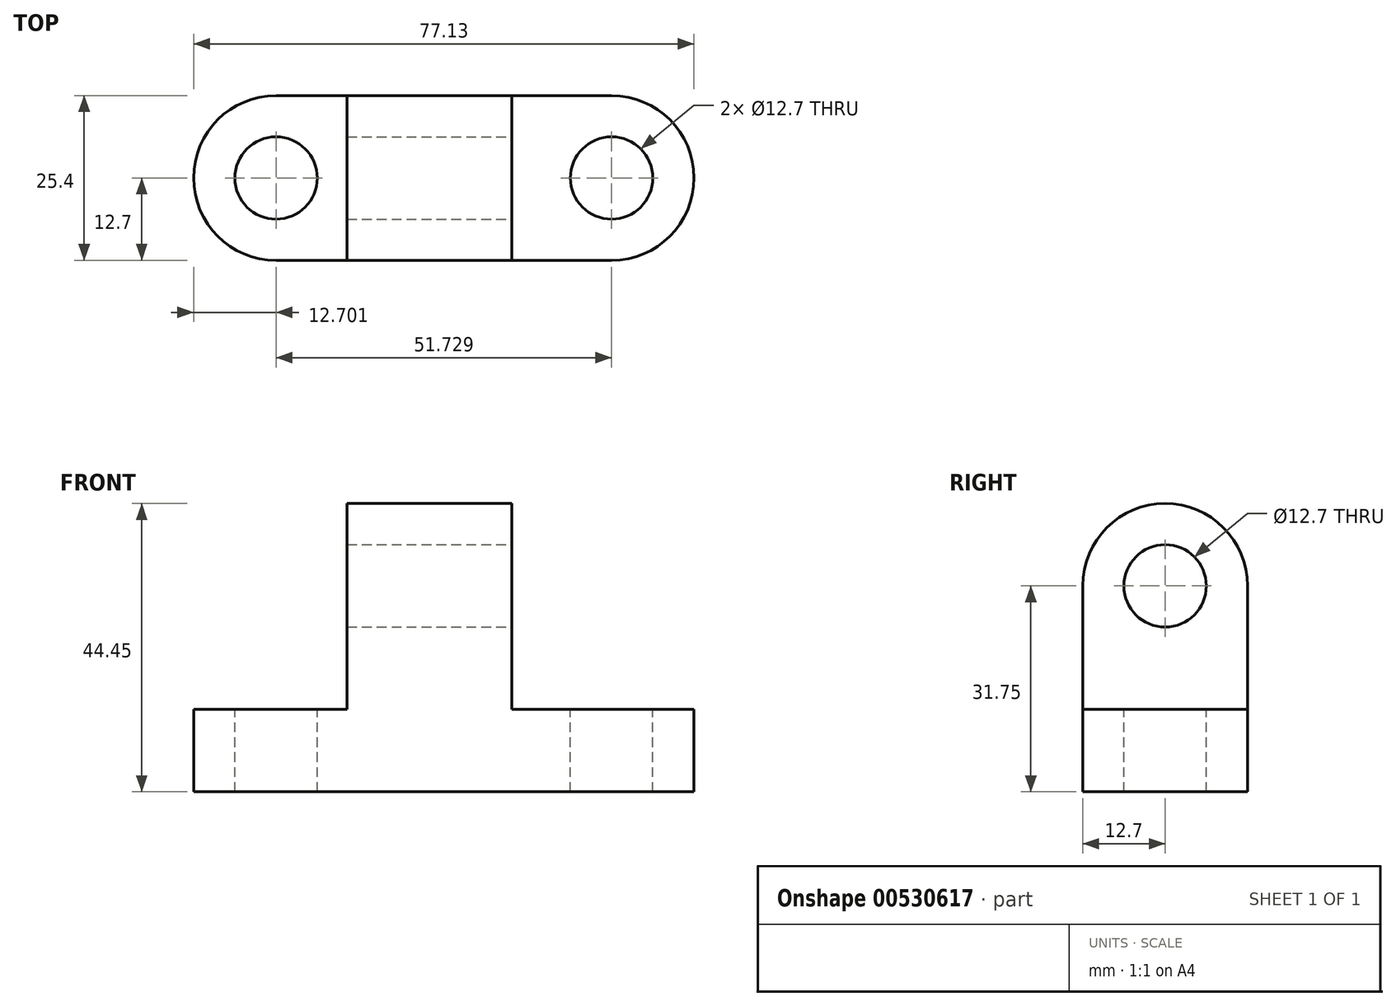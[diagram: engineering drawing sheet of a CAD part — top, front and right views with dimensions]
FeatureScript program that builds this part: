
annotation { "Feature Type Name" : "Feature", "Feature Type Description" : "" }
export const myFeature = defineFeature(function(context is Context, id is Id, definition is map)
    precondition{}
    {
        {
            var Q0;
            Q0=qCreatedBy(makeId("Front.planeOp"),FACE);
            var sketch = newSketch(context, id + "F0", { "sketchPlane" : qUnion([Q0])});
            skLineSegment(sketch, "E0", {"start": v(0, 0) * mm, "end": v(-51.73, 0) * mm});
            skLineSegment(sketch, "E1", {"start": v(-51.73, 0) * mm, "end": v(-51.73, 12.7) * mm});
            skLineSegment(sketch, "E2", {"start": v(-51.73, 12.7) * mm, "end": v(0, 12.7) * mm});
            skLineSegment(sketch, "E3", {"start": v(0, 12.7) * mm, "end": v(0, 0) * mm});
            skSolve(sketch);
        }
        {
            var Q0;
            Q0 = qSketchRegion(id + "F0", true);
            extrude(context, id + "F1", {"entities" : qUnion([Q0]), "depth" : 25.4 * mm, "offsetDistance" : 25.4 * mm});
        }
        {
            var Q0;
            Q0=makeQuery(id+"F1.opExtrude","SWEPT_FACE",FACE,{"disambiguationData":[OSD([sQuery(id+"F0.wireOp",EDGE,"E2")])]});
            var sketch = newSketch(context, id + "F2", { "sketchPlane" : qUnion([Q0])});
            skArc(sketch, "E4", {"start": v(0, -25.4) * mm, "mid": v(12.7, -12.7) * mm, "end": v(0, 0) * mm});
            skArc(sketch, "E5", {"start": v(-51.73, 0) * mm, "mid": v(-64.43, -12.7) * mm, "end": v(-51.73, -25.4) * mm});
            skSolve(sketch);
        }
        {
            var Q0;
            Q0=makeQuery(id+"F2.imprint","IMPRINT",FACE,{"disambiguationData":[TD([[makeQuery(id+"F2.imprint","IMPRINT",EDGE,{"derivedFrom":sQuery(id+"F2.wireOp",EDGE,"E5")}),1.0]])]});
            var Q1;
            Q1=makeQuery(id+"F2.imprint","IMPRINT",FACE,{"disambiguationData":[TD([[makeQuery(id+"F2.imprint","IMPRINT",EDGE,{"derivedFrom":sQuery(id+"F2.wireOp",EDGE,"E4")}),1.0]])]});
            extrude(context, id + "F3", {"entities" : qUnion([Q0, Q1]), "operationType" : NewBodyOperationType.ADD, "oppositeDirection" : true, "depth" : 12.7 * mm, "offsetDistance" : 25.4 * mm});
        }
        {
            var Q0;
            Q0 = qSketchRegion(id + "F0", true);
            extrude(context, id + "F4", {"entities" : qUnion([Q0]), "operationType" : NewBodyOperationType.ADD, "depth" : 25.4 * mm, "offsetDistance" : 25.4 * mm});
        }
        {
            var Q0;
            {var subQ0=sQuery(id+"F0.wireOp",EDGE,"E2");Q0=makeQuery(id+"F3.boolean.opBoolean","MERGE",FACE,{"derivedFrom":[makeQuery(id+"F1.opExtrude","SWEPT_FACE",FACE,{"disambiguationData":[OSD([subQ0])]}),makeQuery(id+"F3.opExtrude","CAP_FACE",FACE,{"disambiguationData":[OSD([subQ0,sQuery(id+"F0.wireOp",EDGE,"E3"),sQuery(id+"F2.wireOp",EDGE,"E4")])],"isStart":true}),makeQuery(id+"F3.opExtrude","CAP_FACE",FACE,{"disambiguationData":[OSD([sQuery(id+"F0.wireOp",EDGE,"E1"),subQ0,sQuery(id+"F2.wireOp",EDGE,"E5")])],"isStart":true})]});}
            var sketch = newSketch(context, id + "F5", { "sketchPlane" : qUnion([Q0])});
            skLineSegment(sketch, "E6", {"start": v(-40.8, 0) * mm, "end": v(-40.8, -25.4) * mm});
            skLineSegment(sketch, "E7", {"start": v(-40.8, -25.4) * mm, "end": v(-15.4, -25.4) * mm});
            skLineSegment(sketch, "E8", {"start": v(-15.4, -25.4) * mm, "end": v(-15.4, 0) * mm});
            skLineSegment(sketch, "E9", {"start": v(-15.4, 0) * mm, "end": v(-40.8, 0) * mm});
            skSolve(sketch);
        }
        {
            var Q0;
            Q0 = qSketchRegion(id + "F5", true);
            extrude(context, id + "F6", {"entities" : qUnion([Q0]), "operationType" : NewBodyOperationType.ADD, "depth" : 19.05 * mm, "offsetDistance" : 25.4 * mm});
        }
        {
            var Q0;
            Q0=makeQuery(id+"F6.opExtrude","SWEPT_FACE",FACE,{"disambiguationData":[OSD([sQuery(id+"F5.wireOp",EDGE,"E8")])]});
            var sketch = newSketch(context, id + "F7", { "sketchPlane" : qUnion([Q0])});
            skArc(sketch, "E10", {"start": v(0, 31.75) * mm, "mid": v(-12.7, 44.45) * mm, "end": v(-25.4, 31.75) * mm});
            skSolve(sketch);
        }
        {
            var Q0;
            Q0 = qSketchRegion(id + "F7", true);
            var Q1;
            Q1=makeQuery(id+"F7.imprint","IMPRINT",FACE,{"disambiguationData":[TD([[makeQuery(id+"F7.imprint","IMPRINT",EDGE,{"derivedFrom":sQuery(id+"F7.wireOp",EDGE,"E10")}),1.0]])]});
            extrude(context, id + "F8", {"entities" : qUnion([Q0, Q1]), "operationType" : NewBodyOperationType.ADD, "oppositeDirection" : true, "depth" : 25.4 * mm, "offsetDistance" : 25.4 * mm});
        }
        {
            var Q0;
            {var subQ0=sQuery(id+"F5.wireOp",EDGE,"E8");Q0=makeQuery(id+"F8.boolean.opBoolean","MERGE",FACE,{"derivedFrom":[makeQuery(id+"F6.opExtrude","SWEPT_FACE",FACE,{"disambiguationData":[OSD([subQ0])]}),makeQuery(id+"F8.opExtrude","CAP_FACE",FACE,{"disambiguationData":[OSD([subQ0,sQuery(id+"F7.wireOp",EDGE,"E10")])],"isStart":true})]});}
            var sketch = newSketch(context, id + "F9", { "sketchPlane" : qUnion([Q0])});
            skCircle(sketch, "E11", {"center": v(-12.7, 31.75) * mm, "radius": 6.35 * mm});
            skSolve(sketch);
        }
        {
            var Q0;
            Q0 = qSketchRegion(id + "F9", true);
            extrude(context, id + "F10", {"entities" : qUnion([Q0]), "operationType" : NewBodyOperationType.REMOVE, "oppositeDirection" : true, "depth" : 25.4 * mm, "offsetDistance" : 25.4 * mm});
        }
        {
            var Q0;
            {var subQ0=sQuery(id+"F2.wireOp",EDGE,"E4");var subQ1=sQuery(id+"F0.wireOp",EDGE,"E3");var subQ2=sQuery(id+"F0.wireOp",EDGE,"E2");var subQ3=sQuery(id+"F0.wireOp",EDGE,"E1");Q0=makeQuery(id+"F6.boolean.opBoolean","SPLIT",FACE,{"disambiguationData":[TD([makeQuery(id+"F3.opExtrude","SWEPT_FACE",FACE,{"disambiguationData":[OSD([subQ0])]})])],"derivedFrom":makeQuery(id+"F3.boolean.opBoolean","MERGE",FACE,{"derivedFrom":[makeQuery(id+"F1.opExtrude","SWEPT_FACE",FACE,{"disambiguationData":[OSD([subQ2])]}),makeQuery(id+"F3.opExtrude","CAP_FACE",FACE,{"disambiguationData":[OSD([subQ2,subQ1,subQ0])],"isStart":true}),makeQuery(id+"F3.opExtrude","CAP_FACE",FACE,{"disambiguationData":[OSD([subQ3,subQ2,sQuery(id+"F2.wireOp",EDGE,"E5")])],"isStart":true})]})});}
            var sketch = newSketch(context, id + "F11", { "sketchPlane" : qUnion([Q0])});
            skCircle(sketch, "E12", {"center": v(0, -12.7) * mm, "radius": 6.35 * mm});
            skSolve(sketch);
        }
        {
            var Q0;
            Q0 = qSketchRegion(id + "F11", true);
            extrude(context, id + "F12", {"entities" : qUnion([Q0]), "operationType" : NewBodyOperationType.REMOVE, "oppositeDirection" : true, "depth" : 25.4 * mm, "offsetDistance" : 25.4 * mm});
        }
        {
            var Q0;
            {var subQ0=sQuery(id+"F0.wireOp",EDGE,"E3");var subQ1=sQuery(id+"F0.wireOp",EDGE,"E2");var subQ2=sQuery(id+"F0.wireOp",EDGE,"E1");var subQ4=sQuery(id+"F2.wireOp",EDGE,"E5");Q0=makeQuery(id+"F6.boolean.opBoolean","SPLIT",FACE,{"disambiguationData":[TD([makeQuery(id+"F3.opExtrude","SWEPT_FACE",FACE,{"disambiguationData":[OSD([subQ4])]})])],"derivedFrom":makeQuery(id+"F3.boolean.opBoolean","MERGE",FACE,{"derivedFrom":[makeQuery(id+"F1.opExtrude","SWEPT_FACE",FACE,{"disambiguationData":[OSD([subQ1])]}),makeQuery(id+"F3.opExtrude","CAP_FACE",FACE,{"disambiguationData":[OSD([subQ1,subQ0,sQuery(id+"F2.wireOp",EDGE,"E4")])],"isStart":true}),makeQuery(id+"F3.opExtrude","CAP_FACE",FACE,{"disambiguationData":[OSD([subQ2,subQ1,subQ4])],"isStart":true})]})});}
            var sketch = newSketch(context, id + "F13", { "sketchPlane" : qUnion([Q0])});
            skCircle(sketch, "E13", {"center": v(-51.73, -12.7) * mm, "radius": 6.35 * mm});
            skSolve(sketch);
        }
        {
            var Q0;
            Q0=makeQuery(id+"F13.imprint","IMPRINT",FACE,{"disambiguationData":[TD([[makeQuery(id+"F13.imprint","IMPRINT",EDGE,{"derivedFrom":sQuery(id+"F13.wireOp",EDGE,"E13")}),1.0]])]});
            extrude(context, id + "F14", {"entities" : qUnion([Q0]), "operationType" : NewBodyOperationType.REMOVE, "oppositeDirection" : true, "depth" : 25.4 * mm, "offsetDistance" : 25.4 * mm});
        }
    });
